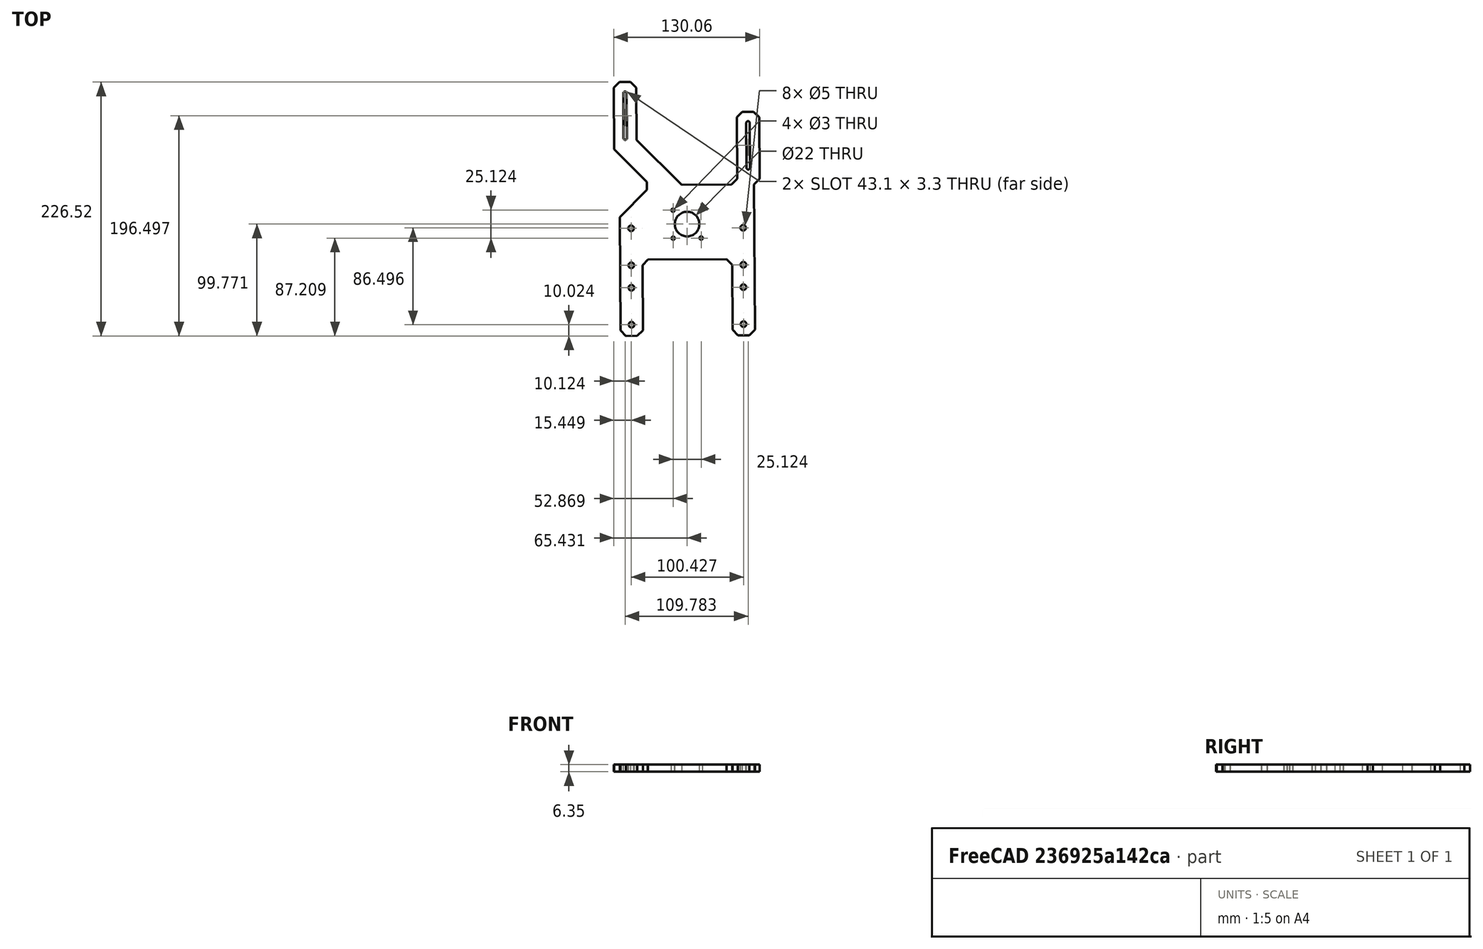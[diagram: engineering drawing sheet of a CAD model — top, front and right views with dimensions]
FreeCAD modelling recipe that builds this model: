
FCSTD DOCUMENT  (FreeCAD 0.21R33771 (Git))
Label: Upper Plate
License: All rights reserved
LicenseURL: http://en.wikipedia.org/wiki/All_rights_reserved
objects: PartDesign::CoordinateSystem×8, Sketcher::SketchObject×1, PartDesign::Pad×1, PartDesign::Body×1
note: 12 computed .brp shape members not serialized (recipe doc carries the construction recipe); baked Part::Feature solids carry a one-line shape summary decoded from their .brp

FEATURE [Sketcher::SketchObject] Sketch015
  FullyConstrained = true
  MapMode = 5
  Placement = pos=(0,0,0) rot=(1,0,0;3.14159rad)
  expr: Constraints[116] = (16 mm - 6.35 mm) / 2
  sketch-geometry (71):
    g0: Circle CenterX=-50 CenterY=89.5 CenterZ=0 NormalX=0 NormalY=0 NormalZ=1 AngleXU=0 Radius=2.5
    g1: Circle CenterX=-50 CenterY=36.5 CenterZ=0 NormalX=0 NormalY=0 NormalZ=1 AngleXU=0 Radius=2.5
    g2: Circle CenterX=50 CenterY=36.5 CenterZ=0 NormalX=0 NormalY=0 NormalZ=1 AngleXU=0 Radius=2.5
    g3: LineSegment StartX=-50 StartY=89.5 StartZ=0 EndX=50 EndY=36.5 EndZ=0
    g4: LineSegment StartX=50 StartY=89.5 StartZ=0 EndX=-50 EndY=36.5 EndZ=0
    g5: GeomPoint X=6.1e-15 Y=63 Z=0
    g6: ArcOfCircle CenterX=-54.825 CenterY=-77 CenterZ=0 NormalX=0 NormalY=0 NormalZ=1 AngleXU=0 Radius=1.55 StartAngle=1.5e-15 EndAngle=3.14159
    g7: ArcOfCircle CenterX=-54.825 CenterY=-117 CenterZ=0 NormalX=0 NormalY=0 NormalZ=1 AngleXU=0 Radius=1.55 StartAngle=3.14159 EndAngle=6.28319
    g8: LineSegment StartX=-56.375 StartY=-77 StartZ=0 EndX=-56.375 EndY=-117 EndZ=0
    g9: LineSegment StartX=-53.275 StartY=-117 StartZ=0 EndX=-53.275 EndY=-77 EndZ=0
    g10: Circle CenterX=0 CenterY=0 CenterZ=0 NormalX=0 NormalY=0 NormalZ=1 AngleXU=0 Radius=11
    g11: GeomPoint X=-53.275 Y=-97 Z=0
    g12: Circle CenterX=50 CenterY=89.5 CenterZ=0 NormalX=0 NormalY=0 NormalZ=1 AngleXU=0 Radius=2.5
    g13: GeomPoint X=0 Y=0 Z=0
    g14: LineSegment StartX=-60 StartY=-6.5 StartZ=0 EndX=-60 EndY=94.5 EndZ=0
    g15: LineSegment StartX=-55 StartY=99.5 StartZ=0 EndX=-45 EndY=99.5 EndZ=0
    g16: LineSegment StartX=-40 StartY=94.5 StartZ=0 EndX=-40 EndY=36.5 EndZ=0
    g17: LineSegment StartX=-40 StartY=36.5 StartZ=0 EndX=-35 EndY=31.5 EndZ=0
    g18: LineSegment StartX=-35 StartY=31.5 StartZ=0 EndX=35 EndY=31.5 EndZ=0
    g19: LineSegment StartX=35 StartY=31.5 StartZ=0 EndX=40 EndY=36.5 EndZ=0
    g20: LineSegment StartX=40 StartY=36.5 StartZ=0 EndX=40 EndY=94.5 EndZ=0
    g21: LineSegment StartX=40 StartY=94.5 StartZ=0 EndX=45 EndY=99.5 EndZ=0
    g22: LineSegment StartX=45 StartY=99.5 StartZ=0 EndX=55 EndY=99.5 EndZ=0
    g23: LineSegment StartX=55 StartY=99.5 StartZ=0 EndX=60 EndY=94.5 EndZ=0
    g24: LineSegment StartX=-44.825 StartY=-75.2843 StartZ=0 EndX=-44.825 EndY=-122 EndZ=0
    g25: LineSegment StartX=-44.825 StartY=-122 StartZ=0 EndX=-49.825 EndY=-127 EndZ=0
    g26: LineSegment StartX=-49.825 StartY=-127 StartZ=0 EndX=-59.825 EndY=-127 EndZ=0
    g27: LineSegment StartX=-59.825 StartY=-127 StartZ=0 EndX=-64.825 EndY=-122 EndZ=0
    g28: LineSegment StartX=-64.825 StartY=-122 StartZ=0 EndX=-64.825 EndY=-67 EndZ=0
    g29: LineSegment StartX=-35.698 StartY=-37.873 StartZ=0 EndX=-35.698 EndY=-30.802 EndZ=0
    g30: LineSegment StartX=-35.698 StartY=-30.802 StartZ=0 EndX=-60 EndY=-6.5 EndZ=0
    g31: LineSegment StartX=-55 StartY=99.5 StartZ=0 EndX=-60 EndY=94.5 EndZ=0
    g32: LineSegment StartX=-45 StartY=99.5 StartZ=0 EndX=-40 EndY=94.5 EndZ=0
    g33: LineSegment StartX=-55 StartY=99.5 StartZ=0 EndX=-50 EndY=89.5 EndZ=0
    g34: LineSegment StartX=-50 StartY=89.5 StartZ=0 EndX=-45 EndY=99.5 EndZ=0
    g35: LineSegment StartX=-64.825 StartY=-67 StartZ=0 EndX=-35.698 EndY=-37.873 EndZ=0
    g36: LineSegment StartX=-54.825 StartY=-77 StartZ=0 EndX=-54.825 EndY=-117 EndZ=0
    g37: Circle CenterX=-12.5 CenterY=12.5 CenterZ=0 NormalX=0 NormalY=0 NormalZ=1 AngleXU=0 Radius=1.5
    g38: Circle CenterX=12.5 CenterY=12.5 CenterZ=0 NormalX=0 NormalY=0 NormalZ=1 AngleXU=0 Radius=1.5
    g39: Circle CenterX=12.5 CenterY=-12.5 CenterZ=0 NormalX=0 NormalY=0 NormalZ=1 AngleXU=0 Radius=1.5
    g40: Circle CenterX=-12.5 CenterY=-12.5 CenterZ=0 NormalX=0 NormalY=0 NormalZ=1 AngleXU=0 Radius=1.5
    g41: LineSegment StartX=-12.5 StartY=12.5 StartZ=0 EndX=12.5 EndY=12.5 EndZ=0
    g42: LineSegment StartX=12.5 StartY=12.5 StartZ=0 EndX=12.5 EndY=-12.5 EndZ=0
    g43: ArcOfCircle CenterX=54.825 CenterY=-50 CenterZ=0 NormalX=0 NormalY=0 NormalZ=1 AngleXU=0 Radius=1.55 StartAngle=3e-16 EndAngle=3.14159
    g44: ArcOfCircle CenterX=54.825 CenterY=-90 CenterZ=0 NormalX=0 NormalY=0 NormalZ=1 AngleXU=0 Radius=1.55 StartAngle=3.14159 EndAngle=6.28319
    g45: LineSegment StartX=53.275 StartY=-50 StartZ=0 EndX=53.275 EndY=-90 EndZ=0
    g46: LineSegment StartX=56.375 StartY=-90 StartZ=0 EndX=56.375 EndY=-50 EndZ=0
    g47: LineSegment StartX=54.825 StartY=-50 StartZ=0 EndX=54.825 EndY=-90 EndZ=0
    g48: GeomPoint X=54.825 Y=-70 Z=0
    g49: LineSegment StartX=-54.825 StartY=-77 StartZ=0 EndX=-50 EndY=-77 EndZ=0
    g50: LineSegment StartX=54.825 StartY=-50 StartZ=0 EndX=50 EndY=-50 EndZ=0
    g51: LineSegment StartX=-44.825 StartY=-75.2843 StartZ=0 EndX=-4.71573 EndY=-35.175 EndZ=0
    g52: LineSegment StartX=64.825 StartY=-95 StartZ=0 EndX=59.825 EndY=-100 EndZ=0
    g53: LineSegment StartX=59.825 StartY=-100 StartZ=0 EndX=49.825 EndY=-100 EndZ=0
    g54: LineSegment StartX=49.825 StartY=-100 StartZ=0 EndX=44.825 EndY=-95 EndZ=0
    g55: LineSegment StartX=44.825 StartY=-95 StartZ=0 EndX=44.825 EndY=-40.175 EndZ=0
    g56: LineSegment StartX=44.825 StartY=-40.175 StartZ=0 EndX=39.825 EndY=-35.175 EndZ=0
    g57: LineSegment StartX=39.825 StartY=-35.175 StartZ=0 EndX=-4.71573 EndY=-35.175 EndZ=0
    g58: LineSegment StartX=64.825 StartY=-40 StartZ=0 EndX=64.825 EndY=-95 EndZ=0
    g59: LineSegment StartX=60 StartY=-35.175 StartZ=0 EndX=64.825 EndY=-40 EndZ=0
    g60: LineSegment StartX=-50 StartY=56.5 StartZ=0 EndX=50 EndY=3.5 EndZ=0
    g61: LineSegment StartX=50 StartY=56.5 StartZ=0 EndX=-50 EndY=3.5 EndZ=0
    g62: GeomPoint X=0 Y=30 Z=0
    g63: GeomPoint X=0 Y=30 Z=0
    g64: LineSegment StartX=-50 StartY=89.5 StartZ=0 EndX=-50 EndY=36.5 EndZ=0
    g65: LineSegment StartX=50 StartY=56.5 StartZ=0 EndX=50 EndY=3.5 EndZ=0
    g66: Circle CenterX=-50 CenterY=3.5 CenterZ=0 NormalX=0 NormalY=0 NormalZ=1 AngleXU=0 Radius=2.5
    g67: Circle CenterX=-50 CenterY=56.5 CenterZ=0 NormalX=0 NormalY=0 NormalZ=1 AngleXU=0 Radius=2.5
    g68: Circle CenterX=50 CenterY=56.5 CenterZ=0 NormalX=0 NormalY=0 NormalZ=1 AngleXU=0 Radius=2.5
    g69: Circle CenterX=50 CenterY=3.5 CenterZ=0 NormalX=0 NormalY=0 NormalZ=1 AngleXU=0 Radius=2.5
    g70: LineSegment StartX=60 StartY=94.5 StartZ=0 EndX=60 EndY=-35.175 EndZ=0
  constraints (179):
    c: Equal(g2,g1)
    c: Equal(g1,g0)
    c: Vertical(g0,g1)
    c: Horizontal(g1,g2)
    c: Coincident(g3,g0)
    c: Coincident(g3,g2)
    c: Coincident(g4,g1)
    c: PointOnObject(g5,g4)
    c: PointOnObject(g5,g3)
    c: DistanceY(g-1,g5) = 63
    c: Tangent(g6,g8) = -1.5708
    c: Tangent(g8,g7) = -1.5708
    c: Tangent(g7,g9) = -1.5708
    c: Tangent(g9,g6) = -1.5708
    c: Equal(g6,g7)
    c: Vertical(g8)
    c: Diameter(g6) = 3.1
    c: DistanceY(g9,g9) = 40
    c: Coincident(g10,g-1)
    c: Diameter(g10) = 22
    c: Symmetric(g6,g7,g11)
    c: DistanceY(g11,g5) = 160
    c: Coincident(g12,g4)
    c: Equal(g2,g12)
    c: Coincident(g13,g10)
    c: Vertical(g14)
    c: Horizontal(g15)
    c: Vertical(g16)
    c: Coincident(g16,g17)
    c: Coincident(g17,g18)
    c: Horizontal(g18)
    c: Coincident(g18,g19)
    c: Coincident(g19,g20)
    c: Vertical(g20)
    c: Coincident(g20,g21)
    c: Coincident(g21,g22)
    c: Horizontal(g22)
    c: Coincident(g22,g23)
    c: Coincident(g24,g25)
    c: Coincident(g25,g26)
    c: Horizontal(g26)
    c: Coincident(g26,g27)
    c: Coincident(g27,g28)
    c: Vertical(g28)
    c: Vertical(g29)
    c: Coincident(g30,g14)
    c: Coincident(g15,g32)
    c: Coincident(g16,g32)
    c: Coincident(g15,g31)
    c: Coincident(g14,g31)
    c: Horizontal(g15,g21)
    c: Horizontal(g23,g20)
    c: Horizontal(g19,g16)
    c: Vertical(g24)
    c: Equal(g17,g32)
    c: Equal(g32,g31)
    c: Equal(g31,g19)
    c: DistanceY(g14,g15) = 5
    c: DistanceX(g14,g15) = 5
    c: Equal(g23,g21)
    c: Equal(g21,g32)
    c: Angle(g19,g18) = 2.35619
    c: Symmetric(g20,g16,g-2)
    c: Symmetric(g23,g14,g-2)
    c: Coincident(g33,g15)
    c: Coincident(g33,g0)
    c: Coincident(g34,g0)
    c: Coincident(g34,g15)
    c: Equal(g34,g33)
    c: Symmetric(g12,g0,g-2)
    c: DistanceY(g12,g22) = 10
    c: DistanceX(g0,g12) = 100
    c: Equal(g25,g27)
    c: Equal(g27,g31)
    c: DistanceX(g27,g24) = 20
    c: Coincident(g35,g28)
    c: Coincident(g35,g29)
    c: Diameter(g12) = 5
    c: Coincident(g30,g29)
    c: Vertical(g12,g2)
    c: Angle(g25,g26) = 2.35619
    c: DistanceY(g25,g7) = 10
    c: DistanceY(g2,g12) = 53
    c: DistanceY(g6,g28) = 10
    c: Coincident(g36,g6)
    c: Coincident(g36,g7)
    c: Symmetric(g24,g27,g36)
    c: Angle(g28,g35) = 2.35619
    c: Vertical(g39,g38)
    c: Horizontal(g39,g40)
    c: Symmetric(g39,g37,g10)
    c: Symmetric(g38,g40,g10)
    c: Coincident(g41,g37)
    c: Coincident(g41,g38)
    c: Coincident(g42,g38)
    c: Coincident(g42,g39)
    c: Equal(g42,g41)
    c: Equal(g38,g39)
    c: Equal(g38,g40)
    c: Equal(g38,g37)
    c: Diameter(g38) = 3
    c: DistanceY(g42,g42) = 25
    c: Angle(g30,g14) = 2.35619
    c: Tangent(g43,g45) = -1.5708
    c: Tangent(g45,g44) = -1.5708
    c: Tangent(g44,g46) = -1.5708
    c: Tangent(g46,g43) = -1.5708
    c: Equal(g43,g44)
    c: Vertical(g45)
    c: Equal(g6,g43)
    c: Coincident(g47,g43)
    c: Coincident(g47,g44)
    c: Symmetric(g44,g43,g48)
    c: Coincident(g49,g6)
    c: Horizontal(g49)
    c: Vertical(g49,g1)
    c: DistanceX(g49,g49) = 4.825
    c: Coincident(g50,g43)
    c: Horizontal(g50)
    c: Equal(g50,g49)
    c: Vertical(g50,g2)
    c: Coincident(g51,g24)
    c: Coincident(g58,g52)
    c: Coincident(g52,g53)
    c: Horizontal(g53)
    c: Coincident(g53,g54)
    c: Coincident(g54,g55)
    c: Vertical(g55)
    c: Coincident(g55,g56)
    c: Coincident(g56,g57)
    c: Coincident(g51,g57)
    c: Parallel(g51,g35)
    c: Parallel(g56,g30)
    c: Equal(g54,g52)
    c: Equal(g52,g25)
    c: Parallel(g54,g56)
    c: DistanceX(g54,g58) = 20
    c: DistanceY(g52,g44) = 10
    c: Symmetric(g58,g54,g47)
    c: Distance(g29,g51) = 20
    c: Horizontal(g57)
    c: Equal(g56,g52)
    c: Coincident(g59,g58)
    c: Vertical(g58)
    c: DistanceX(g20,g23) = 20
    c: Parallel(g59,g56)
    c: DistanceY(g43,g58) = 10
    c: DistanceY(g47,g47) = 40
    c: PointOnObject(g62,g61)
    c: PointOnObject(g63,g60)
    c: Coincident(g63,g62)
    c: PointOnObject(g62,g-2)
    c: Vertical(g61,g60)
    c: Vertical(g60,g0)
    c: Vertical(g60,g61)
    c: Vertical(g61,g12)
    c: Coincident(g64,g0)
    c: Coincident(g64,g1)
    c: Coincident(g65,g61)
    c: Coincident(g65,g60)
    c: Equal(g65,g64)
    c: Coincident(g66,g61)
    c: Coincident(g67,g60)
    c: Coincident(g68,g61)
    c: Coincident(g69,g60)
    c: Equal(g66,g67)
    c: Equal(g67,g68)
    c: Equal(g68,g69)
    c: Equal(g69,g2)
    c: DistanceY(g48,g62) = 100
    c: Horizontal(g69,g66)
    c: DistanceY(g48,g10) = 70
    c: Equal(g29,g56)
    c: Horizontal(g56,g59)
    c: Horizontal(g2,g19)
    c: Coincident(g70,g23)
    c: Coincident(g70,g59)
    c: Vertical(g70)
    c: DistanceY(g14,g66) = 10
FEATURE [PartDesign::Pad] Pad
  Direction = (0,-1e-16,-1)
  Length = 6.35
  Length2 = 10
  Profile = -> Sketch015
  ReferenceAxis = -> Sketch015 [N_Axis]
  Type = 0
FEATURE [PartDesign::CoordinateSystem] Local_CS
  AttacherType = Attacher::AttachEngine3D
  MapMode = 11
  Placement = pos=(0,-1e-15,-6.35) rot=(0.707107,-0.707107,0;3.14159rad)
  Support = -> [Pad]
FEATURE [PartDesign::CoordinateSystem] Local_CS001
  AttacherType = Attacher::AttachEngine3D
  MapMode = 45
  Placement = pos=(50,-63,0) rot=(0,0,1;0rad)
  Support = -> [Pad]
FEATURE [PartDesign::CoordinateSystem] Local_CS002
  AttacherType = Attacher::AttachEngine3D
  MapMode = 45
  Placement = pos=(-50,-63,0) rot=(0,0,1;0rad)
  Support = -> [Pad]
FEATURE [PartDesign::CoordinateSystem] Local_CS003
  AttacherType = Attacher::AttachEngine3D
  MapMode = 45
  Placement = pos=(-50,-30,-6.35) rot=(0,0,1;0rad)
  Support = -> [Pad]
FEATURE [PartDesign::CoordinateSystem] Local_CS004
  AttacherType = Attacher::AttachEngine3D
  MapMode = 45
  Placement = pos=(50,-30,-6.35) rot=(0,0,1;0rad)
  Support = -> [Pad]
FEATURE [PartDesign::CoordinateSystem] Local_CS005
  AttacherType = Attacher::AttachEngine3D
  MapMode = 45
  Placement = pos=(-1.8e-15,4e-16,-3.175) rot=(0,0,1;0rad)
  Support = -> [Pad]
FEATURE [PartDesign::CoordinateSystem] Local_CS006
  AttacherType = Attacher::AttachEngine3D
  AttachmentOffset = pos=(0,0,0) rot=(1,0,0;3.14159rad)
  MapMode = 45
  Placement = pos=(-54.825,97,-6.35) rot=(1,0,0;3.14159rad)
  Support = -> [Pad]
FEATURE [PartDesign::CoordinateSystem] Local_CS007
  AttacherType = Attacher::AttachEngine3D
  AttachmentOffset = pos=(0,0,0) rot=(1,0,0;3.14159rad)
  MapMode = 45
  Placement = pos=(54.825,70,-6.35) rot=(1,0,0;3.14159rad)
  Support = -> [Pad]
FEATURE [PartDesign::Body] Body004  label="Upper Plate"
  Group = -> [Sketch015,Pad,Local_CS,Local_CS001,Local_CS002,Local_CS003,Local_CS004,Local_CS005,Local_CS006,Local_CS007]
  Origin = -> Origin012
  Placement = pos=(45.0712,-32.9487,1.77801) rot=(0,0,1;0.004976rad)
  Tip = -> Pad
